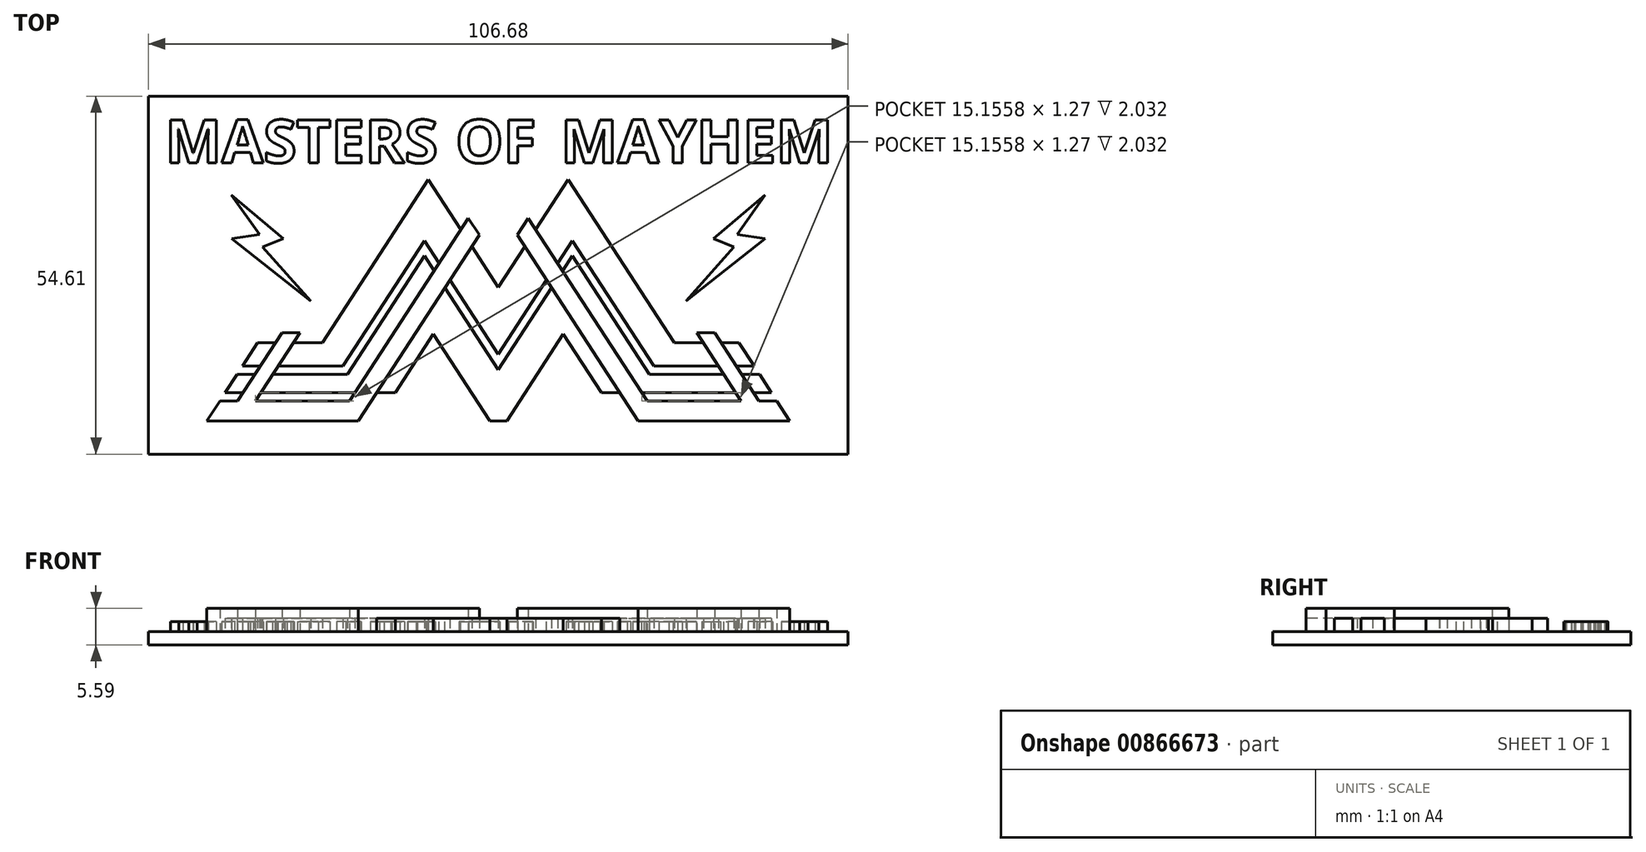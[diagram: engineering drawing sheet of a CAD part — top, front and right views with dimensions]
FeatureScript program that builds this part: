
annotation { "Feature Type Name" : "Feature", "Feature Type Description" : "" }
export const myFeature = defineFeature(function(context is Context, id is Id, definition is map)
    precondition{}
    {
        {
            var Q0;
            Q0=qCreatedBy(makeId("Top.planeOp"),FACE);
            cPlane(context, id + "F0", {"entities" : qUnion([Q0]), "cplaneType" : CPlaneType.OFFSET, "offset" : 2.03 * mm, "width" : 152.4 * mm, "height" : 152.4 * mm});
        }
        {
            var Q0;
            Q0=qCreatedBy(makeId("Top.planeOp"),FACE);
            var sketch = newSketch(context, id + "F1", { "sketchPlane" : qUnion([Q0])});
            skLineSegment(sketch, "E0", {"start": v(0, 58.7) * mm, "end": v(0, -20.32) * mm});
            skLineSegment(sketch, "E1", {"start": v(-59.69, 0) * mm, "end": v(59.69, 0) * mm});
            skLineSegment(sketch, "E2", {"start": v(44.45, 58.7) * mm, "end": v(44.45, -20.32) * mm});
            skSolve(sketch);
        }
        {
            var Q0;
            Q0=qCreatedBy(id+"F0.planeOp",FACE);
            var sketch = newSketch(context, id + "F2", { "sketchPlane" : qUnion([Q0])});
            skLineSegment(sketch, "E3", {"start": v(0, 20.4) * mm, "end": v(10.67, 36.83) * mm});
            skLineSegment(sketch, "E4", {"start": v(10.67, 36.83) * mm, "end": v(26.84, 11.92) * mm});
            skLineSegment(sketch, "E5", {"start": v(26.84, 11.92) * mm, "end": v(36.7, 11.92) * mm});
            skLineSegment(sketch, "E6", {"start": v(36.7, 11.92) * mm, "end": v(44.45, 0) * mm, "construction": true});
            skLineSegment(sketch, "E7", {"start": v(0, 10.14) * mm, "end": v(11.27, 27.5) * mm});
            skLineSegment(sketch, "E8", {"start": v(11.27, 27.5) * mm, "end": v(23.7, 8.37) * mm});
            skLineSegment(sketch, "E9", {"start": v(23.7, 8.37) * mm, "end": v(39.02, 8.37) * mm});
            skLineSegment(sketch, "E10", {"start": v(36.7, 11.92) * mm, "end": v(39.02, 8.37) * mm});
            skLineSegment(sketch, "E11.MirrorCS", {"start": v(-36.7, 11.92) * mm, "end": v(-39.02, 8.37) * mm});
            skLineSegment(sketch, "E12.MirrorCS", {"start": v(-23.7, 8.37) * mm, "end": v(-39.02, 8.37) * mm});
            skLineSegment(sketch, "E13.MirrorCS", {"start": v(-11.27, 27.5) * mm, "end": v(-23.7, 8.37) * mm});
            skLineSegment(sketch, "E14.MirrorCS", {"start": v(0, 10.14) * mm, "end": v(-11.27, 27.5) * mm});
            skLineSegment(sketch, "E15.MirrorCS", {"start": v(0, 20.4) * mm, "end": v(-10.67, 36.83) * mm});
            skLineSegment(sketch, "E16.MirrorCS", {"start": v(-10.67, 36.83) * mm, "end": v(-26.84, 11.92) * mm});
            skLineSegment(sketch, "E17.MirrorCS", {"start": v(-26.84, 11.92) * mm, "end": v(-36.7, 11.92) * mm});
            skSolve(sketch);
        }
        {
            var Q0;
            Q0=qCreatedBy(id+"F0.planeOp",FACE);
            var sketch = newSketch(context, id + "F3", { "sketchPlane" : qUnion([Q0])});
            skLineSegment(sketch, "E18", {"start": v(36.67, 11.99) * mm, "end": v(44.45, 0) * mm, "construction": true});
            skLineSegment(sketch, "E19", {"start": v(44.45, 0) * mm, "end": v(21.34, 0) * mm});
            skLineSegment(sketch, "E20", {"start": v(21.34, 0) * mm, "end": v(2.9, 28.38) * mm});
            skLineSegment(sketch, "E21", {"start": v(2.9, 28.38) * mm, "end": v(4.57, 30.94) * mm});
            skLineSegment(sketch, "E22", {"start": v(4.57, 30.94) * mm, "end": v(22.69, 3.05) * mm});
            skLineSegment(sketch, "E23", {"start": v(22.69, 3.05) * mm, "end": v(37.02, 3.05) * mm});
            skLineSegment(sketch, "E24", {"start": v(42.47, 3.05) * mm, "end": v(44.45, 0) * mm});
            skLineSegment(sketch, "E25.MirrorCS", {"start": v(-2.9, 28.38) * mm, "end": v(-4.57, 30.94) * mm});
            skLineSegment(sketch, "E26.MirrorCS", {"start": v(-4.57, 30.94) * mm, "end": v(-22.69, 3.05) * mm});
            skLineSegment(sketch, "E27.MirrorCS", {"start": v(-22.69, 3.05) * mm, "end": v(-37.02, 3.05) * mm});
            skLineSegment(sketch, "E28.MirrorCS", {"start": v(-42.47, 3.05) * mm, "end": v(-44.45, 0) * mm});
            skLineSegment(sketch, "E29.MirrorCS", {"start": v(-44.45, 0) * mm, "end": v(-21.34, 0) * mm});
            skLineSegment(sketch, "E30.MirrorCS", {"start": v(-21.34, 0) * mm, "end": v(-2.9, 28.38) * mm});
            skLineSegment(sketch, "E31", {"start": v(39.74, 3.05) * mm, "end": v(33, 13.45) * mm});
            skLineSegment(sketch, "E32", {"start": v(33, 13.45) * mm, "end": v(30.27, 13.45) * mm});
            skLineSegment(sketch, "E33", {"start": v(30.27, 13.45) * mm, "end": v(37.02, 3.05) * mm});
            skLineSegment(sketch, "E34.trimOffspring", {"start": v(39.74, 3.05) * mm, "end": v(42.47, 3.05) * mm});
            skLineSegment(sketch, "E35.MirrorCS", {"start": v(-39.74, 3.05) * mm, "end": v(-33, 13.45) * mm});
            skLineSegment(sketch, "E36.MirrorCS", {"start": v(-33, 13.45) * mm, "end": v(-30.27, 13.45) * mm});
            skLineSegment(sketch, "E37.MirrorCS", {"start": v(-30.27, 13.45) * mm, "end": v(-37.02, 3.05) * mm});
            skLineSegment(sketch, "E38.trimOffspring", {"start": v(-39.74, 3.05) * mm, "end": v(-42.47, 3.05) * mm});
            skSolve(sketch);
        }
        {
            var Q0;
            Q0=qCreatedBy(id+"F0.planeOp",FACE);
            var sketch = newSketch(context, id + "F4", { "sketchPlane" : qUnion([Q0])});
            skLineSegment(sketch, "E39", {"start": v(36.7, 11.92) * mm, "end": v(44.45, 0) * mm, "construction": true});
            skLineSegment(sketch, "E40", {"start": v(41.65, 4.32) * mm, "end": v(39.84, 7.1) * mm, "construction": true});
            skLineSegment(sketch, "E41", {"start": v(39.84, 7.1) * mm, "end": v(24.53, 7.1) * mm, "construction": true});
            skLineSegment(sketch, "E42", {"start": v(41.65, 4.32) * mm, "end": v(26.33, 4.32) * mm, "construction": true});
            skLineSegment(sketch, "E43", {"start": v(26.33, 4.32) * mm, "end": v(24.53, 7.1) * mm, "construction": true});
            skLineSegment(sketch, "E44.MirrorCS", {"start": v(-39.84, 7.1) * mm, "end": v(-24.53, 7.1) * mm, "construction": true});
            skLineSegment(sketch, "E45.MirrorCS", {"start": v(-26.33, 4.32) * mm, "end": v(-24.53, 7.1) * mm, "construction": true});
            skLineSegment(sketch, "E46.MirrorCS", {"start": v(-41.65, 4.32) * mm, "end": v(-26.33, 4.32) * mm, "construction": true});
            skLineSegment(sketch, "E47.MirrorCS", {"start": v(-41.65, 4.32) * mm, "end": v(-39.84, 7.1) * mm, "construction": true});
            skSolve(sketch);
        }
        {
            var Q0;
            Q0=qCreatedBy(id+"F0.planeOp",FACE);
            var sketch = newSketch(context, id + "F5", { "sketchPlane" : qUnion([Q0])});
            skLineSegment(sketch, "E48", {"start": v(11.27, 25.17) * mm, "end": v(23.01, 7.1) * mm});
            skLineSegment(sketch, "E49", {"start": v(24.82, 4.32) * mm, "end": v(15.72, 4.32) * mm});
            skLineSegment(sketch, "E50", {"start": v(15.72, 4.32) * mm, "end": v(9.9, 13.27) * mm});
            skLineSegment(sketch, "E51", {"start": v(9.9, 13.27) * mm, "end": v(1.29, 0) * mm});
            skLineSegment(sketch, "E52", {"start": v(11.27, 25.17) * mm, "end": v(0, 7.81) * mm});
            skLineSegment(sketch, "E53", {"start": v(1.29, 0) * mm, "end": v(0, 0) * mm});
            skLineSegment(sketch, "E54.MirrorCS", {"start": v(-24.82, 4.32) * mm, "end": v(-15.72, 4.32) * mm});
            skLineSegment(sketch, "E55.MirrorCS", {"start": v(-11.27, 25.17) * mm, "end": v(-23.01, 7.1) * mm});
            skLineSegment(sketch, "E56.MirrorCS", {"start": v(-11.27, 25.17) * mm, "end": v(0, 7.81) * mm});
            skLineSegment(sketch, "E57.MirrorCS", {"start": v(-15.72, 4.32) * mm, "end": v(-9.9, 13.27) * mm});
            skLineSegment(sketch, "E58.MirrorCS", {"start": v(-9.9, 13.27) * mm, "end": v(-1.29, 0) * mm});
            skLineSegment(sketch, "E59.MirrorCS", {"start": v(-1.29, 0) * mm, "end": v(0, 0) * mm});
            skLineSegment(sketch, "E60", {"start": v(-23.01, 7.1) * mm, "end": v(-39.84, 7.1) * mm});
            skLineSegment(sketch, "E61", {"start": v(-39.84, 7.1) * mm, "end": v(-41.65, 4.32) * mm});
            skLineSegment(sketch, "E62", {"start": v(-41.65, 4.32) * mm, "end": v(-24.82, 4.32) * mm});
            skPoint(sketch, "E63.orphan", {"position": v(-24.82, 4.32) * mm});
            skLineSegment(sketch, "E64", {"start": v(24.82, 4.32) * mm, "end": v(41.65, 4.32) * mm});
            skLineSegment(sketch, "E65", {"start": v(41.65, 4.32) * mm, "end": v(39.84, 7.1) * mm});
            skLineSegment(sketch, "E66", {"start": v(39.84, 7.1) * mm, "end": v(23.01, 7.1) * mm});
            skSolve(sketch);
        }
        {
            var Q0;
            Q0=qCreatedBy(makeId("Top.planeOp"),FACE);
            var sketch = newSketch(context, id + "F6", { "sketchPlane" : qUnion([Q0])});
            skLineSegment(sketch, "E67.bottom", {"start": v(-53.34, 49.53) * mm, "end": v(53.34, 49.53) * mm});
            skLineSegment(sketch, "E67.top", {"start": v(-53.34, -5.08) * mm, "end": v(53.34, -5.08) * mm});
            skLineSegment(sketch, "E67.left", {"start": v(-53.34, 49.53) * mm, "end": v(-53.34, -5.08) * mm});
            skLineSegment(sketch, "E67.right", {"start": v(53.34, 49.53) * mm, "end": v(53.34, -5.08) * mm});
            skPoint(sketch, "E68", {"position": v(49.38, 0) * mm});
            skPoint(sketch, "E69", {"position": v(0, 49.53) * mm});
            skSolve(sketch);
        }
        {
            var Q0;
            Q0=makeQuery(id+"F2.imprint","IMPRINT",FACE,{"disambiguationData":[TD([[makeQuery(id+"F2.imprint","IMPRINT",EDGE,{"derivedFrom":sQuery(id+"F2.wireOp",EDGE,"E3")}),-1.0]])]});
            extrude(context, id + "F7", {"entities" : qUnion([Q0]), "depth" : 2.03 * mm, "offsetDistance" : 25.4 * mm});
        }
        {
            var Q0;
            Q0=makeQuery(id+"F5.imprint","IMPRINT",FACE,{"disambiguationData":[TD([[makeQuery(id+"F5.imprint","IMPRINT",EDGE,{"derivedFrom":sQuery(id+"F5.wireOp",EDGE,"E48")}),-1.0]])]});
            extrude(context, id + "F8", {"entities" : qUnion([Q0]), "operationType" : NewBodyOperationType.ADD, "depth" : 2.03 * mm, "offsetDistance" : 25.4 * mm});
        }
        {
            var Q0;
            Q0=makeQuery(id+"F3.imprint","IMPRINT",FACE,{"disambiguationData":[TD([[makeQuery(id+"F3.imprint","IMPRINT",EDGE,{"derivedFrom":sQuery(id+"F3.wireOp",EDGE,"E25.MirrorCS")}),1.0]])]});
            var Q1;
            Q1=makeQuery(id+"F3.imprint","IMPRINT",FACE,{"disambiguationData":[TD([[makeQuery(id+"F3.imprint","IMPRINT",EDGE,{"derivedFrom":sQuery(id+"F3.wireOp",EDGE,"E19")}),-1.0]])]});
            extrude(context, id + "F9", {"entities" : qUnion([Q0, Q1]), "operationType" : NewBodyOperationType.ADD, "depth" : 3.56 * mm, "offsetDistance" : 25.4 * mm});
        }
        {
            var Q0;
            Q0=makeQuery(id+"F6.imprint","IMPRINT",FACE,{"disambiguationData":[TD([[makeQuery(id+"F6.imprint","IMPRINT",EDGE,{"derivedFrom":sQuery(id+"F6.wireOp",EDGE,"E67.bottom")}),-1.0]])]});
            extrude(context, id + "F10", {"entities" : qUnion([Q0]), "operationType" : NewBodyOperationType.ADD, "depth" : 2.03 * mm, "offsetDistance" : 25.4 * mm});
        }
        {
            var Q0;
            Q0=qCreatedBy(id+"F0.planeOp",FACE);
            var Q1;
            Q1=qCreatedBy(id+"F0.planeOp",FACE);
            var Q2;
            Q2=qCreatedBy(id+"F0.planeOp",FACE);
            var sketch = newSketch(context, id + "F11", { "sketchPlane" : qUnion([Q0, Q1, Q2])});
            skText(sketch, "E70", { "text": "MASTERS", "fontName": "OpenSans-Bold.ttf"});
            const initialGuessF11  = {"E70": [-0.0508, 0.03937, 1, 0, 0.0066]};
            skSetInitialGuess(sketch, initialGuessF11);
            skSolve(sketch);
        }
        {
            var Q0;
            Q0=qCreatedBy(id+"F0.planeOp",FACE);
            var Q1;
            Q1=qCreatedBy(id+"F0.planeOp",FACE);
            var sketch = newSketch(context, id + "F12", { "sketchPlane" : qUnion([Q0, Q1])});
            skText(sketch, "E71", { "text": "MAYHEM", "fontName": "OpenSans-Bold.ttf"});
            const initialGuessF12  = {"E71": [0.00953, 0.03937, 1, 0, 0.0066]};
            skSetInitialGuess(sketch, initialGuessF12);
            skSolve(sketch);
        }
        {
            var Q0;
            Q0=qCreatedBy(id+"F0.planeOp",FACE);
            var sketch = newSketch(context, id + "F13", { "sketchPlane" : qUnion([Q0])});
            skText(sketch, "E72", { "text": "OF", "fontName": "OpenSans-Bold.ttf"});
            const initialGuessF13  = {"E72": [-0.00653, 0.03937, 1, 0, 0.0066]};
            skSetInitialGuess(sketch, initialGuessF13);
            skSolve(sketch);
        }
        {
            var Q0;
            Q0 = qSketchRegion(id + "F11", true);
            var Q1;
            Q1 = qSketchRegion(id + "F13", true);
            var Q2;
            Q2 = qSketchRegion(id + "F12", true);
            extrude(context, id + "F14", {"entities" : qUnion([Q0, Q1, Q2]), "operationType" : NewBodyOperationType.ADD, "depth" : 1.52 * mm, "offsetDistance" : 25.4 * mm});
        }
        {
            var Q0;
            Q0=qCreatedBy(id+"F0.planeOp",FACE);
            var sketch = newSketch(context, id + "F15", { "sketchPlane" : qUnion([Q0])});
            skLineSegment(sketch, "E73", {"start": v(40.7, 34.5) * mm, "end": v(32.79, 27.83) * mm});
            skLineSegment(sketch, "E74", {"start": v(32.79, 27.83) * mm, "end": v(35.94, 26.55) * mm});
            skLineSegment(sketch, "E75", {"start": v(35.94, 26.55) * mm, "end": v(28.62, 18.26) * mm});
            skLineSegment(sketch, "E76", {"start": v(28.62, 18.26) * mm, "end": v(40.68, 27.83) * mm});
            skLineSegment(sketch, "E77", {"start": v(40.68, 27.83) * mm, "end": v(36.43, 28.42) * mm});
            skLineSegment(sketch, "E78", {"start": v(36.43, 28.42) * mm, "end": v(40.7, 34.5) * mm});
            skLineSegment(sketch, "E79.MirrorCS", {"start": v(-40.7, 34.5) * mm, "end": v(-32.79, 27.83) * mm});
            skLineSegment(sketch, "E80.MirrorCS", {"start": v(-36.43, 28.42) * mm, "end": v(-40.7, 34.5) * mm});
            skLineSegment(sketch, "E81.MirrorCS", {"start": v(-40.68, 27.83) * mm, "end": v(-36.43, 28.42) * mm});
            skLineSegment(sketch, "E82.MirrorCS", {"start": v(-28.62, 18.26) * mm, "end": v(-40.68, 27.83) * mm});
            skLineSegment(sketch, "E83.MirrorCS", {"start": v(-35.94, 26.55) * mm, "end": v(-28.62, 18.26) * mm});
            skLineSegment(sketch, "E84.MirrorCS", {"start": v(-32.79, 27.83) * mm, "end": v(-35.94, 26.55) * mm});
            skSolve(sketch);
        }
        {
            var Q0;
            Q0 = qSketchRegion(id + "F15", true);
            extrude(context, id + "F16", {"entities" : qUnion([Q0]), "operationType" : NewBodyOperationType.ADD, "depth" : 2.03 * mm, "offsetDistance" : 25.4 * mm});
        }
    });
